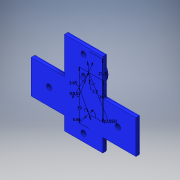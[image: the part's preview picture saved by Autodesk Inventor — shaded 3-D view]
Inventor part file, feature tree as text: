
AUTODESK INVENTOR PART (.ipt)
format: ipt  version: 2016 (Build 200138000, 138)  size: 268,288 bytes
history: native  units: in
note: dims shown in document units (in); Inventor stores cm internally (conversion verified against a paired STEP export)
features: sketch x6, extrude x4, hole x2, fillet x2
ambient origin geometry x8: Origin, YZ Plane, XZ Plane, XY Plane, X Axis, Y Axis, Z Axis, Center Point
bodies: Solid1 (feature_tree)
feature tree (14):
  extrude  "Extrusion1"  Depth=0.5197in
  extrude  "Extrusion10"  Depth=0.0787in
  extrude  "Extrusion11"  Depth=0.2096in TaperAngle=0.0deg
  hole  "Hole2"  [1 undecoded]
  extrude  "Extrusion12"  Depth=0.2953in
  fillet  "Fillet17"  Radius=0.2953in
  fillet  "Fillet18"  Radius=0.2598in
  hole  "Hole4"  [1 undecoded]
  sketch  "Sketch1"  dims[d0=1.6142in d1=0.5197in]
  sketch  "Sketch15"  dims[d2=0.0787in d3=0.0in d79=0.5118in]
  sketch  "Sketch16"  dims[d80=0.5118in d81=0.2096in d82=0.0in]
  sketch  "Sketch17"  dims[d83=0.5118in d84=0.5118in]
  sketch  "Sketch19"  dims[d85=0.562in d86=0.0in d87=0.2953in d88=0.2953in d89=0.2598in]
  sketch  "Sketch20"  dims[d90=0.2598in d91=0.2756in d92=0.1181in d93=0.2953in d94=0.2953in d95=0.1181in d96=0.2598in d97=0.2598in d98=0.2756in d99=0.0787in d100=0.2362in d101=0.1575in d102=0.0787in d103=90.0deg d104=0.1181in d105=0.8108in d108=0.2835in d109=0.748in d110=0.5358in d111=0.0219in d112=0.3622in d113=0.1437in d114=0.5551in d115=0.2224in d116=0.0787in d119=0.8386in d120=0.1181in d121=0.0in d122=0.1181in d123=0.0354in d131=0.0591in d132=0.2362in d133=0.1575in d134=0.0787in d135=90.0deg d136=0.1575in d137=0.8108in]
note: 2 required parameter values undecoded (feature->parameter linkage not recoverable at this tier; creation-order binding heuristic only, values carry confidence <= 0.55)
